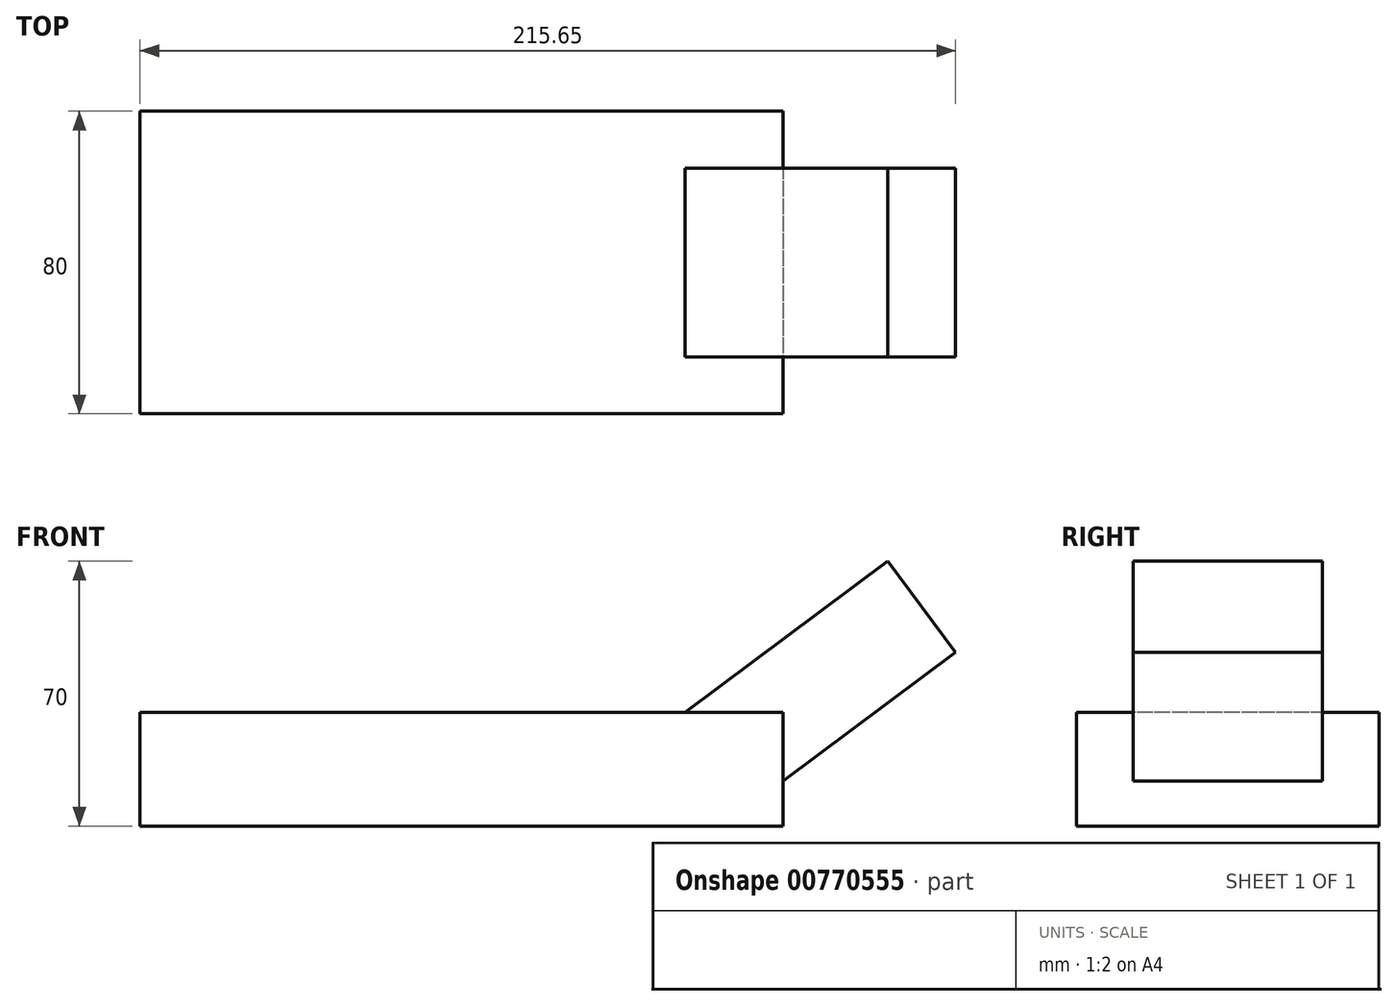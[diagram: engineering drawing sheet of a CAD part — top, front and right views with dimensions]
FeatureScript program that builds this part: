
annotation { "Feature Type Name" : "Feature", "Feature Type Description" : "" }
export const myFeature = defineFeature(function(context is Context, id is Id, definition is map)
    precondition{}
    {
        {
            var Q0;
            Q0=qCreatedBy(makeId("Top.planeOp"),FACE);
            var sketch = newSketch(context, id + "F0", { "sketchPlane" : qUnion([Q0])});
            skLineSegment(sketch, "E0.bottom", {"start": v(-85, 40) * mm, "end": v(85, 40) * mm});
            skLineSegment(sketch, "E0.top", {"start": v(-85, -40) * mm, "end": v(85, -40) * mm});
            skLineSegment(sketch, "E0.left", {"start": v(-85, 40) * mm, "end": v(-85, -40) * mm});
            skLineSegment(sketch, "E0.right", {"start": v(85, 40) * mm, "end": v(85, -40) * mm});
            skSolve(sketch);
        }
        {
            var Q0;
            Q0=makeQuery(id+"F0.imprint","IMPRINT",FACE,{"disambiguationData":[TD([[makeQuery(id+"F0.imprint","IMPRINT",EDGE,{"derivedFrom":sQuery(id+"F0.wireOp",EDGE,"E0.bottom")}),-1.0]])]});
            extrude(context, id + "F1", {"entities" : qUnion([Q0]), "depth" : 30 * mm, "offsetDistance" : 25 * mm});
        }
        {
            var Q0;
            Q0=makeQuery(id+"F1.opExtrude","SWEPT_FACE",FACE,{"disambiguationData":[OSD([sQuery(id+"F0.wireOp",EDGE,"E0.top")])]});
            var sketch = newSketch(context, id + "F2", { "sketchPlane" : qUnion([Q0])});
            skLineSegment(sketch, "E1", {"start": v(59.16, 30) * mm, "end": v(112.7, 70) * mm});
            skLineSegment(sketch, "E2", {"start": v(112.7, 70) * mm, "end": v(130.65, 45.97) * mm});
            skLineSegment(sketch, "E3", {"start": v(130.65, 45.97) * mm, "end": v(85, 11.86) * mm});
            skSolve(sketch);
        }
        {
            var Q0;
            {var subQ5=sQuery(id+"F2.wireOp",EDGE,"E1");Q0=makeQuery(id+"F2.imprint","IMPRINT",FACE,{"disambiguationData":[TD([[makeQuery(id+"F2.imprint","IMPRINT",EDGE,{"derivedFrom":subQ5}),-1.0]])]});}
            extrude(context, id + "F3", {"entities" : qUnion([Q0]), "oppositeDirection" : true, "depth" : 61.7 * mm, "offsetDistance" : 25 * mm});
        }
        {
            var Q0;
            Q0=makeQuery(id+"F3.opExtrude","CAP_FACE",FACE,{"disambiguationData":[OSD([sQuery(id+"F0.wireOp",EDGE,"E0.top"),sQuery(id+"F0.wireOp",EDGE,"E0.right"),sQuery(id+"F2.wireOp",EDGE,"E1"),sQuery(id+"F2.wireOp",EDGE,"E2"),sQuery(id+"F2.wireOp",EDGE,"E3")])],"isStart":true});
            extrude(context, id + "F4", {"entities" : qUnion([Q0]), "operationType" : NewBodyOperationType.REMOVE, "oppositeDirection" : true, "depth" : 14.1 * mm, "offsetDistance" : 25 * mm});
        }
        {
            var Q0;
            Q0=makeQuery(id+"F1.opExtrude","CAP_FACE",FACE,{"disambiguationData":[OSD([sQuery(id+"F0.wireOp",EDGE,"E0.bottom"),sQuery(id+"F0.wireOp",EDGE,"E0.top"),sQuery(id+"F0.wireOp",EDGE,"E0.left"),sQuery(id+"F0.wireOp",EDGE,"E0.right")])],"isStart":false});
            var sketch = newSketch(context, id + "F5", { "sketchPlane" : qUnion([Q0])});
            skLineSegment(sketch, "E4", {"start": v(85, 25) * mm, "end": v(55, 25) * mm, "construction": true});
            skLineSegment(sketch, "E5", {"start": v(55, -25) * mm, "end": v(85, -25) * mm, "construction": true});
            skSolve(sketch);
        }
        {
            var Q0;
            Q0=makeQuery(id+"F3.opExtrude","SWEPT_FACE",FACE,{"disambiguationData":[OSD([sQuery(id+"F2.wireOp",EDGE,"E1")])]});
            var sketch = newSketch(context, id + "F6", { "sketchPlane" : qUnion([Q0])});
            skLineSegment(sketch, "E6", {"start": v(65.35, 25) * mm, "end": v(65.35, -25) * mm, "construction": true});
            skSolve(sketch);
        }
        {
            var Q0;
            Q0=makeQuery(id+"F3.opExtrude","CAP_FACE",FACE,{"disambiguationData":[OSD([sQuery(id+"F0.wireOp",EDGE,"E0.top"),sQuery(id+"F0.wireOp",EDGE,"E0.right"),sQuery(id+"F2.wireOp",EDGE,"E1"),sQuery(id+"F2.wireOp",EDGE,"E2"),sQuery(id+"F2.wireOp",EDGE,"E3")])],"isStart":false});
            var Q1;
            Q1=sQuery(id+"F5.wireOp",VERTEX,"E4.end");
            extrude(context, id + "F7", {"entities" : qUnion([Q0]), "operationType" : NewBodyOperationType.ADD, "endBound" : BoundingType.UP_TO_VERTEX, "depth" : 25 * mm, "endBoundEntityVertex" : qUnion([Q1]), "offsetDistance" : 25 * mm});
        }
        {
            var Q0;
            Q0=makeQuery(id+"F4.boolean.opBoolean","COPY",FACE,{"derivedFrom":makeQuery(id+"F4.opExtrude","CAP_FACE",FACE,{"disambiguationData":[OSD([sQuery(id+"F0.wireOp",EDGE,"E0.top"),sQuery(id+"F0.wireOp",EDGE,"E0.right"),sQuery(id+"F2.wireOp",EDGE,"E1"),sQuery(id+"F2.wireOp",EDGE,"E2"),sQuery(id+"F2.wireOp",EDGE,"E3")])],"isStart":false})});
            var Q1;
            Q1=sQuery(id+"F6.wireOp",VERTEX,"E6.end");
            extrude(context, id + "F8", {"entities" : qUnion([Q0]), "operationType" : NewBodyOperationType.REMOVE, "endBound" : BoundingType.UP_TO_VERTEX, "oppositeDirection" : true, "depth" : 25 * mm, "endBoundEntityVertex" : qUnion([Q1]), "offsetDistance" : 25 * mm});
        }
    });
